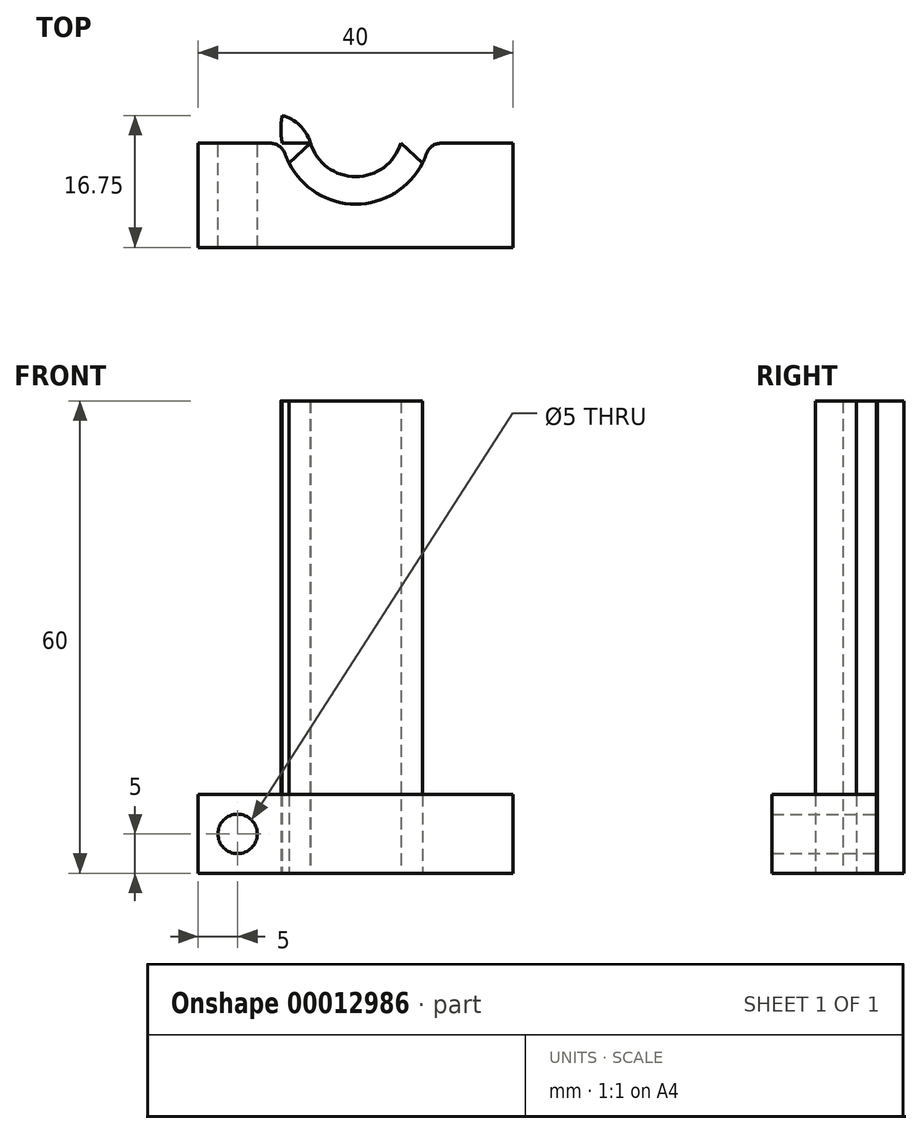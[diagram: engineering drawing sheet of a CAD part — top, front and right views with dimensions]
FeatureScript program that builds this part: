
annotation { "Feature Type Name" : "Feature", "Feature Type Description" : "" }
export const myFeature = defineFeature(function(context is Context, id is Id, definition is map)
    precondition{}
    {
        {
            var Q0;
            Q0=qCreatedBy(makeId("Top.planeOp"),FACE);
            var sketch = newSketch(context, id + "F0", { "sketchPlane" : qUnion([Q0])});
            skCircle(sketch, "E0", {"center": v(0, 0) * mm, "radius": 6 * mm});
            skLineSegment(sketch, "E1.rect.bottom", {"start": v(20, 15) * mm, "end": v(-20, 15) * mm});
            skLineSegment(sketch, "E1.rect.top", {"start": v(20, -15) * mm, "end": v(-20, -15) * mm});
            skLineSegment(sketch, "E1.rect.left", {"start": v(20, 15) * mm, "end": v(20, -15) * mm});
            skLineSegment(sketch, "E1.rect.right", {"start": v(-20, 15) * mm, "end": v(-20, -15) * mm});
            skLineSegment(sketch, "E2.rect.bottom", {"start": v(20, 1.75) * mm, "end": v(5.74, 1.75) * mm});
            skLineSegment(sketch, "E2.rect.top", {"start": v(20, -1.75) * mm, "end": v(10.87, -1.75) * mm});
            skLineSegment(sketch, "E2.rect.left", {"start": v(20, 1.75) * mm, "end": v(20, -1.75) * mm});
            skLineSegment(sketch, "E2.rect.right", {"start": v(-20, 1.75) * mm, "end": v(-20, -1.75) * mm});
            skArc(sketch, "E3", {"start": v(-9.34, 1.75) * mm, "mid": v(-9.5, 0) * mm, "end": v(-9.34, -1.75) * mm});
            skArc(sketch, "E4", {"start": v(-8.98, -3.1) * mm, "mid": v(0, -9.5) * mm, "end": v(8.98, -3.1) * mm});
            skLineSegment(sketch, "E5", {"start": v(-5.74, -1.75) * mm, "end": v(-9.34, -1.75) * mm});
            skLineSegment(sketch, "E6", {"start": v(-5.74, 1.75) * mm, "end": v(-20, 1.75) * mm});
            skLineSegment(sketch, "E7", {"start": v(5.74, 1.75) * mm, "end": v(-5.74, 1.75) * mm});
            skArc(sketch, "E8", {"start": v(9.34, 1.75) * mm, "mid": v(0, 9.5) * mm, "end": v(-9.34, 1.75) * mm});
            skArc(sketch, "E9", {"start": v(9.34, -1.75) * mm, "mid": v(9.5, 0) * mm, "end": v(9.34, 1.75) * mm});
            skLineSegment(sketch, "E10", {"start": v(-10.87, -1.75) * mm, "end": v(-20, -1.75) * mm});
            skPoint(sketch, "E11.visualSharp", {"position": v(-9.34, -1.75) * mm});
            skArc(sketch, "E11.filletArc", {"start": v(-8.98, -3.1) * mm, "mid": v(-9.71, -2.12) * mm, "end": v(-10.87, -1.75) * mm});
            skLineSegment(sketch, "E12", {"start": v(9.34, -1.75) * mm, "end": v(-5.74, -1.75) * mm});
            skPoint(sketch, "E13.visualSharp", {"position": v(9.34, -1.75) * mm});
            skArc(sketch, "E13.filletArc", {"start": v(10.87, -1.75) * mm, "mid": v(9.71, -2.12) * mm, "end": v(8.98, -3.1) * mm});
            skArc(sketch, "E14", {"start": v(-5.74, -1.75) * mm, "mid": v(-7.07, 0.48) * mm, "end": v(-9.34, 1.75) * mm});
            skLineSegment(sketch, "E15", {"start": v(-5.74, 1.75) * mm, "end": v(-20, 15) * mm});
            skLineSegment(sketch, "E16", {"start": v(5.74, 1.75) * mm, "end": v(20, 15) * mm});
            skLineSegment(sketch, "E17", {"start": v(-5.74, -1.75) * mm, "end": v(-20, -15) * mm});
            skLineSegment(sketch, "E18", {"start": v(5.74, -1.75) * mm, "end": v(20, -15) * mm});
            skArc(sketch, "E19.MirrorCS", {"start": v(5.74, 1.75) * mm, "mid": v(7.07, -0.48) * mm, "end": v(9.34, -1.75) * mm});
            skSolve(sketch);
        }
        {
            var Q0;
            {var subQ6=sQuery(id+"F0.wireOp",EDGE,"E10");Q0=makeQuery(id+"F0.imprint","IMPRINT",FACE,{"disambiguationData":[TD([[makeQuery(id+"F0.imprint","IMPRINT",EDGE,{"derivedFrom":subQ6}),1.0]])]});}
            var Q1;
            {var subQ3=sQuery(id+"F0.wireOp",EDGE,"E1.rect.top");Q1=makeQuery(id+"F0.imprint","IMPRINT",FACE,{"disambiguationData":[TD([[makeQuery(id+"F0.imprint","IMPRINT",EDGE,{"derivedFrom":subQ3}),-1.0]])]});}
            var Q2;
            {var subQ6=sQuery(id+"F0.wireOp",EDGE,"E2.rect.top");Q2=makeQuery(id+"F0.imprint","IMPRINT",FACE,{"disambiguationData":[TD([[makeQuery(id+"F0.imprint","IMPRINT",EDGE,{"derivedFrom":subQ6}),1.0]])]});}
            extrude(context, id + "F1", {"entities" : qUnion([Q0, Q1, Q2]), "depth" : 10 * mm});
        }
        {
            var Q0;
            {var subQ8=sQuery(id+"F0.wireOp",EDGE,"E2.rect.right");Q0=makeQuery(id+"F0.imprint","IMPRINT",FACE,{"disambiguationData":[TD([[makeQuery(id+"F0.imprint","IMPRINT",EDGE,{"derivedFrom":subQ8}),1.0]])]});}
            var Q1;
            {var subQ3=sQuery(id+"F0.wireOp",EDGE,"E3");Q1=makeQuery(id+"F0.imprint","IMPRINT",FACE,{"disambiguationData":[TD([[makeQuery(id+"F0.imprint","IMPRINT",EDGE,{"derivedFrom":subQ3}),1.0]])]});}
            var Q2;
            {var subQ1=sQuery(id+"F0.wireOp",EDGE,"E4");var subQ6=sQuery(id+"F0.wireOp",EDGE,"E17");var subQ7=makeQuery(id+"F0.imprint","INTERSECT",VERTEX,{"derivedFrom":[subQ1,subQ6]});Q2=makeQuery(id+"F0.imprint","IMPRINT",FACE,{"disambiguationData":[TD([[makeQuery(id+"F0.imprint","IMPRINT",EDGE,{"disambiguationData":[TD([[subQ7,-1.0]])],"derivedFrom":subQ1}),1.0]])]});}
            extrude(context, id + "F2", {"entities" : qUnion([Q0, Q1, Q2]), "depth" : 60 * mm});
        }
        {
            var Q0;
            Q0=qCreatedBy(makeId("Front.planeOp"),FACE);
            var sketch = newSketch(context, id + "F3", { "sketchPlane" : qUnion([Q0])});
            skLineSegment(sketch, "E20.bottom", {"start": v(0, 0) * mm, "end": v(-15, 0) * mm});
            skLineSegment(sketch, "E20.top", {"start": v(0, 5) * mm, "end": v(-15, 5) * mm});
            skLineSegment(sketch, "E20.left", {"start": v(0, 0) * mm, "end": v(0, 5) * mm});
            skLineSegment(sketch, "E20.right", {"start": v(-15, 0) * mm, "end": v(-15, 5) * mm});
            skCircle(sketch, "E21", {"center": v(-15, 5) * mm, "radius": 2.5 * mm});
            skCircle(sketch, "E22.MirrorC", {"center": v(15, 5) * mm, "radius": 2.5 * mm});
            skSolve(sketch);
        }
        {
            var Q0;
            {var subQ1=sQuery(id+"F3.wireOp",EDGE,"E20.right");var subQ3=sQuery(id+"F3.wireOp",EDGE,"E20.top");var subQ5=makeQuery(id+"F3.imprint","INTERSECT",VERTEX,{"derivedFrom":[subQ3,subQ1]});Q0=makeQuery(id+"F3.imprint","IMPRINT",FACE,{"disambiguationData":[TD([[makeQuery(id+"F3.imprint","IMPRINT",EDGE,{"disambiguationData":[TD([[subQ5,1.0]])],"derivedFrom":subQ3}),-1.0]])]});}
            var Q1;
            {var subQ1=sQuery(id+"F3.wireOp",EDGE,"E20.right");var subQ3=sQuery(id+"F3.wireOp",EDGE,"E20.top");var subQ5=makeQuery(id+"F3.imprint","INTERSECT",VERTEX,{"derivedFrom":[subQ3,subQ1]});Q1=makeQuery(id+"F3.imprint","IMPRINT",FACE,{"disambiguationData":[TD([[makeQuery(id+"F3.imprint","IMPRINT",EDGE,{"disambiguationData":[TD([[subQ5,1.0]])],"derivedFrom":subQ3}),1.0]])]});}
            extrude(context, id + "F4", {"entities" : qUnion([Q0, Q1]), "operationType" : NewBodyOperationType.REMOVE, "endBound" : BoundingType.THROUGH_ALL, "oppositeDirection" : true, "depth" : 25 * mm});
        }
        {
            var Q0;
            Q0=makeQuery(id+"F3.imprint","IMPRINT",FACE,{"disambiguationData":[TD([[makeQuery(id+"F3.imprint","IMPRINT",EDGE,{"derivedFrom":sQuery(id+"F3.wireOp",EDGE,"E22.MirrorC")}),-1.0]])]});
            var Q1;
            {var subQ1=sQuery(id+"F3.wireOp",EDGE,"E20.right");var subQ3=sQuery(id+"F3.wireOp",EDGE,"E20.top");var subQ5=makeQuery(id+"F3.imprint","INTERSECT",VERTEX,{"derivedFrom":[subQ3,subQ1]});Q1=makeQuery(id+"F3.imprint","IMPRINT",FACE,{"disambiguationData":[TD([[makeQuery(id+"F3.imprint","IMPRINT",EDGE,{"disambiguationData":[TD([[subQ5,1.0]])],"derivedFrom":subQ3}),-1.0]])]});}
            var Q2;
            {var subQ1=sQuery(id+"F3.wireOp",EDGE,"E20.right");var subQ3=sQuery(id+"F3.wireOp",EDGE,"E20.top");var subQ5=makeQuery(id+"F3.imprint","INTERSECT",VERTEX,{"derivedFrom":[subQ3,subQ1]});Q2=makeQuery(id+"F3.imprint","IMPRINT",FACE,{"disambiguationData":[TD([[makeQuery(id+"F3.imprint","IMPRINT",EDGE,{"disambiguationData":[TD([[subQ5,1.0]])],"derivedFrom":subQ3}),1.0]])]});}
            var Q3;
            Q3=sQuery(id+"F3.wireOp",EDGE,"E22.MirrorC");
            var Q4;
            Q4=makeQuery(id+"F1.opExtrude","SWEPT_BODY",BODY,{"disambiguationData":[OSD([sQuery(id+"F0.wireOp",EDGE,"E1.rect.top"),sQuery(id+"F0.wireOp",EDGE,"E1.rect.left"),sQuery(id+"F0.wireOp",EDGE,"E1.rect.right"),sQuery(id+"F0.wireOp",EDGE,"E2.rect.top"),sQuery(id+"F0.wireOp",EDGE,"E4"),sQuery(id+"F0.wireOp",EDGE,"E10"),sQuery(id+"F0.wireOp",EDGE,"E11.filletArc"),sQuery(id+"F0.wireOp",EDGE,"E13.filletArc")])]});
            extrude(context, id + "F5", {"entities" : qUnion([Q0, Q1, Q2]), "operationType" : NewBodyOperationType.REMOVE, "surfaceEntities" : qUnion([Q3]), "endBound" : BoundingType.THROUGH_ALL, "endBoundEntityBody" : qUnion([Q4]), "depth" : 25 * mm});
        }
    });
